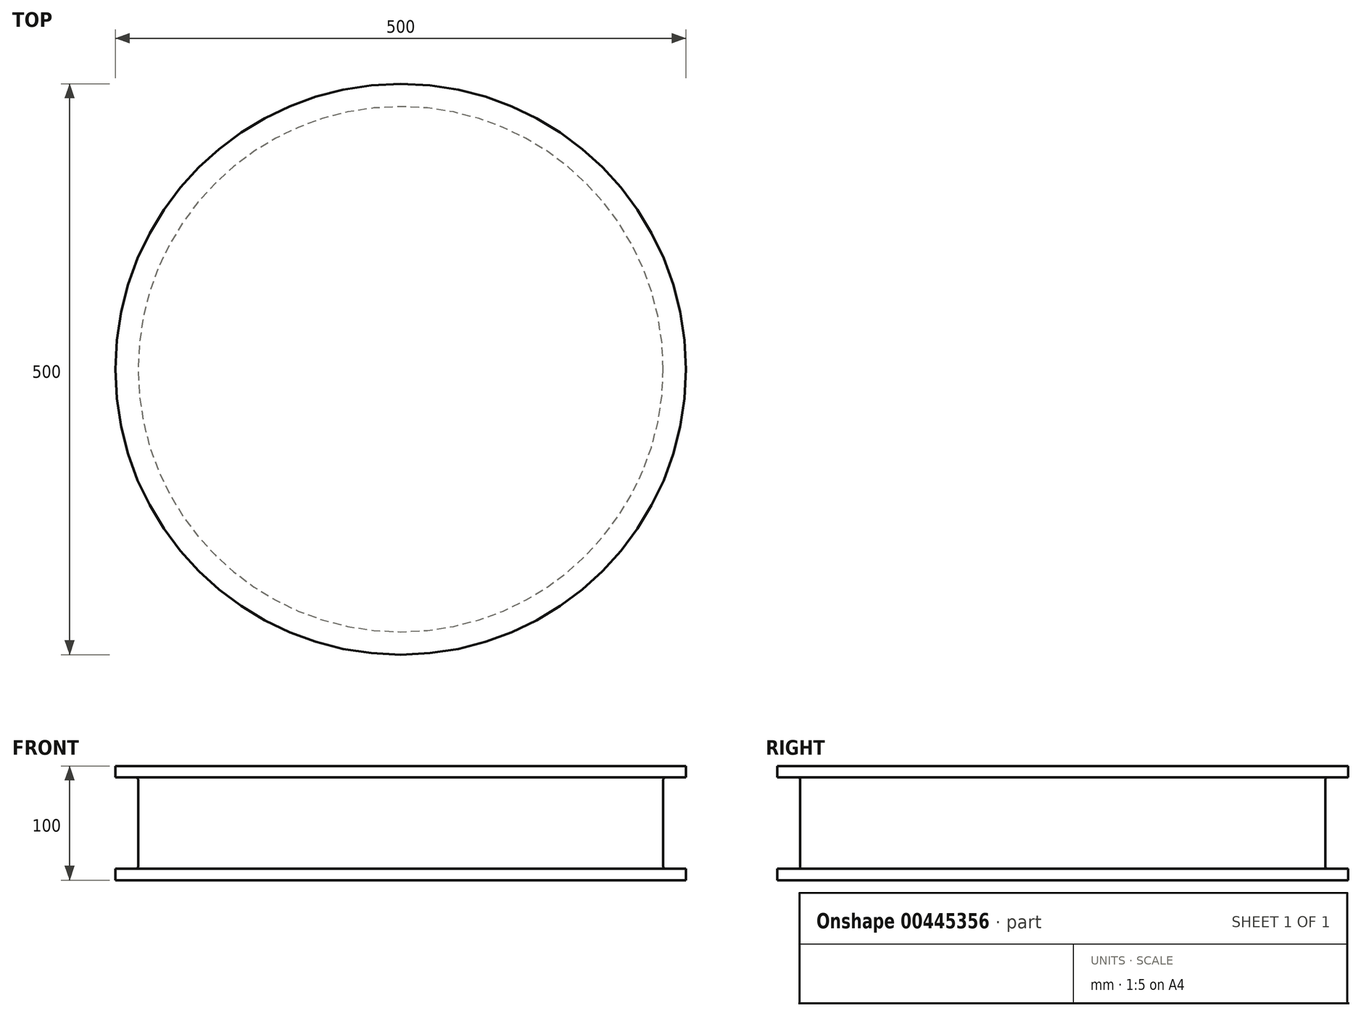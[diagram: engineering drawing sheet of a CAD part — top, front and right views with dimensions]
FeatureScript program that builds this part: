
annotation { "Feature Type Name" : "Feature", "Feature Type Description" : "" }
export const myFeature = defineFeature(function(context is Context, id is Id, definition is map)
    precondition{}
    {
        {
            var Q0;
            Q0=qCreatedBy(makeId("Top.planeOp"),FACE);
            var sketch = newSketch(context, id + "F0", { "sketchPlane" : qUnion([Q0])});
            skCircle(sketch, "E0", {"center": v(0, 0) * mm, "radius": 250 * mm});
            skSolve(sketch);
        }
        {
            var Q0;
            Q0 = qSketchRegion(id + "F0", true);
            extrude(context, id + "F1", {"entities" : qUnion([Q0]), "depth" : 10 * mm});
        }
        {
            var Q0;
            Q0=makeQuery(id+"F1.opExtrude","CAP_FACE",FACE,{"disambiguationData":[OSD([sQuery(id+"F0.wireOp",EDGE,"E0")])],"isStart":false});
            var sketch = newSketch(context, id + "F2", { "sketchPlane" : qUnion([Q0])});
            skCircle(sketch, "E1", {"center": v(0, 0) * mm, "radius": 230 * mm});
            skSolve(sketch);
        }
        {
            var Q0;
            Q0 = qSketchRegion(id + "F2", true);
            extrude(context, id + "F3", {"entities" : qUnion([Q0]), "operationType" : NewBodyOperationType.ADD, "depth" : 80 * mm});
        }
        {
            var Q0;
            Q0=makeQuery(id+"F3.opExtrude","CAP_FACE",FACE,{"disambiguationData":[OSD([sQuery(id+"F2.wireOp",EDGE,"E1")])],"isStart":false});
            var sketch = newSketch(context, id + "F4", { "sketchPlane" : qUnion([Q0])});
            skCircle(sketch, "E2", {"center": v(0, 0) * mm, "radius": 250 * mm});
            skSolve(sketch);
        }
        {
            var Q0;
            Q0 = qSketchRegion(id + "F4", true);
            extrude(context, id + "F5", {"entities" : qUnion([Q0]), "operationType" : NewBodyOperationType.ADD, "depth" : 10 * mm});
        }
        {
            var Q0;
            Q0=makeQuery(id+"F3.opExtrude","SWEPT_FACE",FACE,{"disambiguationData":[OSD([sQuery(id+"F2.wireOp",EDGE,"E1")])]});
            fillet(context, id + "F6", {"entities" : qUnion([Q0]), "radius" : 2 * mm, "tangentPropagation" : true, "allowEdgeOverflow" : false});
        }
    });
